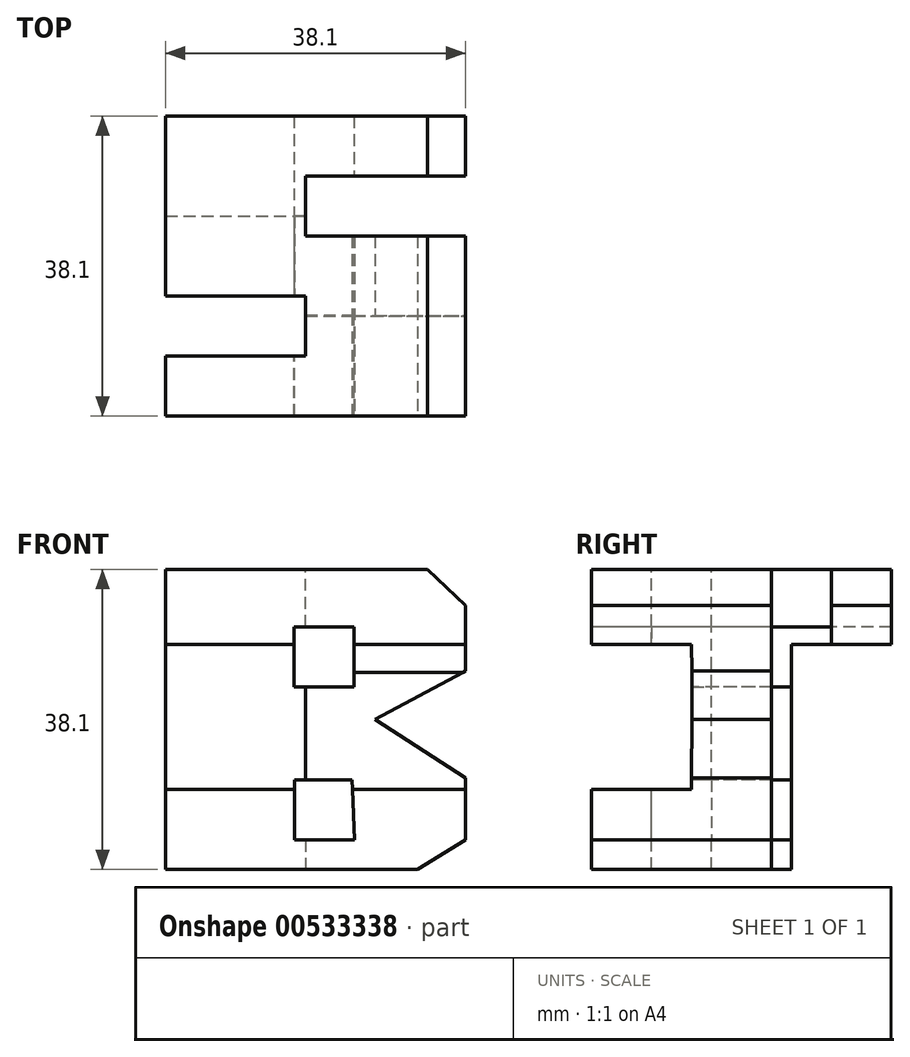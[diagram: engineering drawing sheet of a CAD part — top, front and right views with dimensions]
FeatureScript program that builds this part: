
annotation { "Feature Type Name" : "Feature", "Feature Type Description" : "" }
export const myFeature = defineFeature(function(context is Context, id is Id, definition is map)
    precondition{}
    {
        {
            var Q0;
            Q0=qCreatedBy(makeId("Front.planeOp"),FACE);
            var sketch = newSketch(context, id + "F0", { "sketchPlane" : qUnion([Q0])});
            skLineSegment(sketch, "E0", {"start": v(0, 0) * mm, "end": v(0, 38.1) * mm});
            skLineSegment(sketch, "E1", {"start": v(0, 38.1) * mm, "end": v(38.1, 38.1) * mm});
            skLineSegment(sketch, "E2", {"start": v(38.1, 38.1) * mm, "end": v(38.1, 0) * mm});
            skLineSegment(sketch, "E3", {"start": v(38.1, 0) * mm, "end": v(0, 0) * mm});
            skSolve(sketch);
        }
        {
            var Q0;
            Q0=makeQuery(id+"F0.imprint","IMPRINT",FACE,{"disambiguationData":[TD([[makeQuery(id+"F0.imprint","IMPRINT",EDGE,{"derivedFrom":sQuery(id+"F0.wireOp",EDGE,"E0")}),-1.0]])]});
            extrude(context, id + "F1", {"entities" : qUnion([Q0]), "depth" : 38.1 * mm, "offsetDistance" : 25.4 * mm});
        }
        {
            var Q0;
            Q0=makeQuery(id+"F1.opExtrude","CAP_FACE",FACE,{"disambiguationData":[OSD([sQuery(id+"F0.wireOp",EDGE,"E0"),sQuery(id+"F0.wireOp",EDGE,"E1"),sQuery(id+"F0.wireOp",EDGE,"E2"),sQuery(id+"F0.wireOp",EDGE,"E3")])],"isStart":false});
            cPlane(context, id + "F2", {"entities" : qUnion([Q0]), "cplaneType" : CPlaneType.OFFSET, "offset" : 38.1 * mm, "width" : 152.4 * mm, "height" : 152.4 * mm});
        }
        {
            var Q0;
            Q0=qCreatedBy(makeId("Right.planeOp"),FACE);
            cPlane(context, id + "F3", {"entities" : qUnion([Q0]), "cplaneType" : CPlaneType.OFFSET, "offset" : 38.1 * mm, "width" : 152.4 * mm, "height" : 152.4 * mm});
        }
        {
            var Q0;
            Q0=qCreatedBy(makeId("Top.planeOp"),FACE);
            cPlane(context, id + "F4", {"entities" : qUnion([Q0]), "cplaneType" : CPlaneType.OFFSET, "offset" : 38.1 * mm, "width" : 152.4 * mm, "height" : 152.4 * mm});
        }
        {
            var Q0;
            Q0=qCreatedBy(id+"F3.planeOp",FACE);
            var sketch = newSketch(context, id + "F5", { "sketchPlane" : qUnion([Q0])});
            skLineSegment(sketch, "E4", {"start": v(0, 38.1) * mm, "end": v(0, 0) * mm});
            skLineSegment(sketch, "E5", {"start": v(0, 0) * mm, "end": v(-38.1, 0) * mm});
            skLineSegment(sketch, "E6", {"start": v(-38.1, 0) * mm, "end": v(-38.1, 38.1) * mm});
            skLineSegment(sketch, "E7", {"start": v(-38.1, 38.1) * mm, "end": v(0, 38.1) * mm});
            skLineSegment(sketch, "E8", {"start": v(-25.4, 28.57) * mm, "end": v(-38.1, 28.57) * mm});
            skLineSegment(sketch, "E9", {"start": v(-12.7, 28.57) * mm, "end": v(0, 28.57) * mm});
            skPoint(sketch, "E10.orphan", {"position": v(-19.05, 38.1) * mm});
            skLineSegment(sketch, "E11", {"start": v(-25.4, 28.57) * mm, "end": v(-25.32, 25.02) * mm});
            skPoint(sketch, "E12.orphan", {"position": v(-38.1, 19.05) * mm});
            skPoint(sketch, "E13.end.orphan", {"position": v(-19.05, 0) * mm});
            skPoint(sketch, "E13.start.orphan", {"position": v(-19.05, 19.05) * mm});
            skPoint(sketch, "E14.end.orphan", {"position": v(0, 19.05) * mm});
            skPoint(sketch, "E15.orphan", {"position": v(-19.05, 28.57) * mm});
            skLineSegment(sketch, "E16", {"start": v(-38.1, 0) * mm, "end": v(-38.1, 10.16) * mm});
            skLineSegment(sketch, "E17", {"start": v(-38.1, 10.16) * mm, "end": v(-25.4, 10.16) * mm});
            skLineSegment(sketch, "E18", {"start": v(-25.32, 25.02) * mm, "end": v(-25.4, 10.16) * mm});
            skLineSegment(sketch, "E19", {"start": v(-12.7, 28.57) * mm, "end": v(-12.7, 0) * mm});
            skSolve(sketch);
        }
        {
            var Q0;
            {var subQ3=sQuery(id+"F5.wireOp",EDGE,"E9");Q0=makeQuery(id+"F5.imprint","IMPRINT",FACE,{"disambiguationData":[TD([[makeQuery(id+"F5.imprint","IMPRINT",EDGE,{"derivedFrom":subQ3}),-1.0]])]});}
            var Q1;
            {var subQ1=sQuery(id+"F5.wireOp",EDGE,"E8");Q1=makeQuery(id+"F5.imprint","IMPRINT",FACE,{"disambiguationData":[TD([[makeQuery(id+"F5.imprint","IMPRINT",EDGE,{"derivedFrom":subQ1}),1.0]])]});}
            extrude(context, id + "F6", {"entities" : qUnion([Q0, Q1]), "operationType" : NewBodyOperationType.REMOVE, "oppositeDirection" : true, "depth" : 38.1 * mm, "offsetDistance" : 25.4 * mm});
        }
        {
            var Q0;
            Q0=qCreatedBy(id+"F4.planeOp",FACE);
            var sketch = newSketch(context, id + "F7", { "sketchPlane" : qUnion([Q0])});
            skLineSegment(sketch, "E20", {"start": v(0, 0) * mm, "end": v(0, -38.1) * mm});
            skLineSegment(sketch, "E21", {"start": v(0, -38.1) * mm, "end": v(38.1, -38.1) * mm});
            skLineSegment(sketch, "E22", {"start": v(38.1, -38.1) * mm, "end": v(38.1, 0) * mm});
            skLineSegment(sketch, "E23", {"start": v(38.1, 0) * mm, "end": v(0, 0) * mm});
            skLineSegment(sketch, "E24", {"start": v(38.1, -7.62) * mm, "end": v(17.78, -7.62) * mm});
            skLineSegment(sketch, "E25", {"start": v(17.78, -7.62) * mm, "end": v(17.78, -15.24) * mm});
            skLineSegment(sketch, "E26", {"start": v(17.78, -15.24) * mm, "end": v(38.1, -15.24) * mm});
            skLineSegment(sketch, "E27", {"start": v(0, -22.86) * mm, "end": v(17.78, -22.86) * mm});
            skLineSegment(sketch, "E28", {"start": v(17.78, -22.86) * mm, "end": v(17.78, -30.48) * mm});
            skLineSegment(sketch, "E29", {"start": v(17.78, -30.48) * mm, "end": v(0, -30.48) * mm});
            skSolve(sketch);
        }
        {
            var Q0;
            {var subQ0=sQuery(id+"F7.wireOp",EDGE,"E24");Q0=makeQuery(id+"F7.imprint","IMPRINT",FACE,{"disambiguationData":[TD([[makeQuery(id+"F7.imprint","IMPRINT",EDGE,{"derivedFrom":subQ0}),1.0]])]});}
            var Q1;
            {var subQ0=sQuery(id+"F7.wireOp",EDGE,"E27");Q1=makeQuery(id+"F7.imprint","IMPRINT",FACE,{"disambiguationData":[TD([[makeQuery(id+"F7.imprint","IMPRINT",EDGE,{"derivedFrom":subQ0}),-1.0]])]});}
            extrude(context, id + "F8", {"entities" : qUnion([Q0, Q1]), "operationType" : NewBodyOperationType.REMOVE, "oppositeDirection" : true, "depth" : 38.1 * mm, "offsetDistance" : 25.4 * mm});
        }
        {
            var Q0;
            Q0=qCreatedBy(id+"F2.planeOp",FACE);
            var sketch = newSketch(context, id + "F9", { "sketchPlane" : qUnion([Q0])});
            skLineSegment(sketch, "E30", {"start": v(0, 0) * mm, "end": v(0, 38.1) * mm});
            skLineSegment(sketch, "E31", {"start": v(0, 38.1) * mm, "end": v(38.1, 38.1) * mm});
            skLineSegment(sketch, "E32", {"start": v(38.1, 38.1) * mm, "end": v(38.1, 11.6) * mm});
            skLineSegment(sketch, "E33", {"start": v(38.1, 0) * mm, "end": v(0, 0) * mm});
            skPoint(sketch, "E34.endSnap0", {"position": v(10.16, 19.05) * mm});
            skLineSegment(sketch, "E35", {"start": v(26.6, 19.05) * mm, "end": v(38.1, 11.6) * mm});
            skLineSegment(sketch, "E36", {"start": v(26.6, 19.05) * mm, "end": v(38.1, 25.2) * mm});
            skLineSegment(sketch, "E37", {"start": v(38.1, 25.2) * mm, "end": v(38.1, 33.51) * mm});
            skLineSegment(sketch, "E38", {"start": v(38.1, 33.51) * mm, "end": v(33.28, 38.1) * mm});
            skLineSegment(sketch, "E39", {"start": v(33.28, 38.1) * mm, "end": v(10.16, 38.1) * mm});
            skLineSegment(sketch, "E40", {"start": v(23.9, 23.2) * mm, "end": v(23.9, 30.82) * mm});
            skLineSegment(sketch, "E41", {"start": v(16.4, 11.36) * mm, "end": v(16.4, 3.74) * mm});
            skLineSegment(sketch, "E42", {"start": v(16.4, 3.74) * mm, "end": v(24.02, 3.74) * mm});
            skLineSegment(sketch, "E43", {"start": v(23.9, 23.2) * mm, "end": v(16.29, 23.2) * mm});
            skLineSegment(sketch, "E44", {"start": v(16.29, 23.2) * mm, "end": v(16.29, 30.82) * mm});
            skLineSegment(sketch, "E45", {"start": v(16.29, 30.82) * mm, "end": v(23.9, 30.82) * mm});
            skLineSegment(sketch, "E46", {"start": v(16.4, 11.36) * mm, "end": v(23.67, 11.36) * mm});
            skLineSegment(sketch, "E47", {"start": v(23.67, 11.36) * mm, "end": v(24.02, 3.74) * mm});
            skLineSegment(sketch, "E48", {"start": v(38.1, 3.74) * mm, "end": v(32, 0) * mm});
            skPoint(sketch, "E49.end.orphan", {"position": v(10.16, 0) * mm});
            skPoint(sketch, "E34.start.orphan", {"position": v(10.16, 19.05) * mm});
            skLineSegment(sketch, "E50.trimOffspring", {"start": v(38.1, 3.74) * mm, "end": v(38.1, 0) * mm});
            skSolve(sketch);
        }
        {
            var Q0;
            Q0=makeQuery(id+"F9.imprint","IMPRINT",FACE,{"disambiguationData":[TD([[makeQuery(id+"F9.imprint","IMPRINT",EDGE,{"derivedFrom":sQuery(id+"F9.wireOp",EDGE,"E40")}),1.0]])]});
            var Q1;
            {var subQ3=sQuery(id+"F9.wireOp",EDGE,"E38");Q1=makeQuery(id+"F9.imprint","IMPRINT",FACE,{"disambiguationData":[TD([[makeQuery(id+"F9.imprint","IMPRINT",EDGE,{"derivedFrom":subQ3}),-1.0]])]});}
            var Q2;
            {var subQ0=sQuery(id+"F9.wireOp",EDGE,"E35");Q2=makeQuery(id+"F9.imprint","IMPRINT",FACE,{"disambiguationData":[TD([[makeQuery(id+"F9.imprint","IMPRINT",EDGE,{"derivedFrom":subQ0}),1.0]])]});}
            var Q3;
            {var subQ2=sQuery(id+"F9.wireOp",EDGE,"E48");Q3=makeQuery(id+"F9.imprint","IMPRINT",FACE,{"disambiguationData":[TD([[makeQuery(id+"F9.imprint","IMPRINT",EDGE,{"derivedFrom":subQ2}),1.0]])]});}
            var Q4;
            Q4=makeQuery(id+"F9.imprint","IMPRINT",FACE,{"disambiguationData":[TD([[makeQuery(id+"F9.imprint","IMPRINT",EDGE,{"derivedFrom":sQuery(id+"F9.wireOp",EDGE,"E41")}),1.0]])]});
            extrude(context, id + "F10", {"entities" : qUnion([Q0, Q1, Q2, Q3, Q4]), "operationType" : NewBodyOperationType.REMOVE, "oppositeDirection" : true, "depth" : 76.2 * mm, "offsetDistance" : 25.4 * mm});
        }
    });
